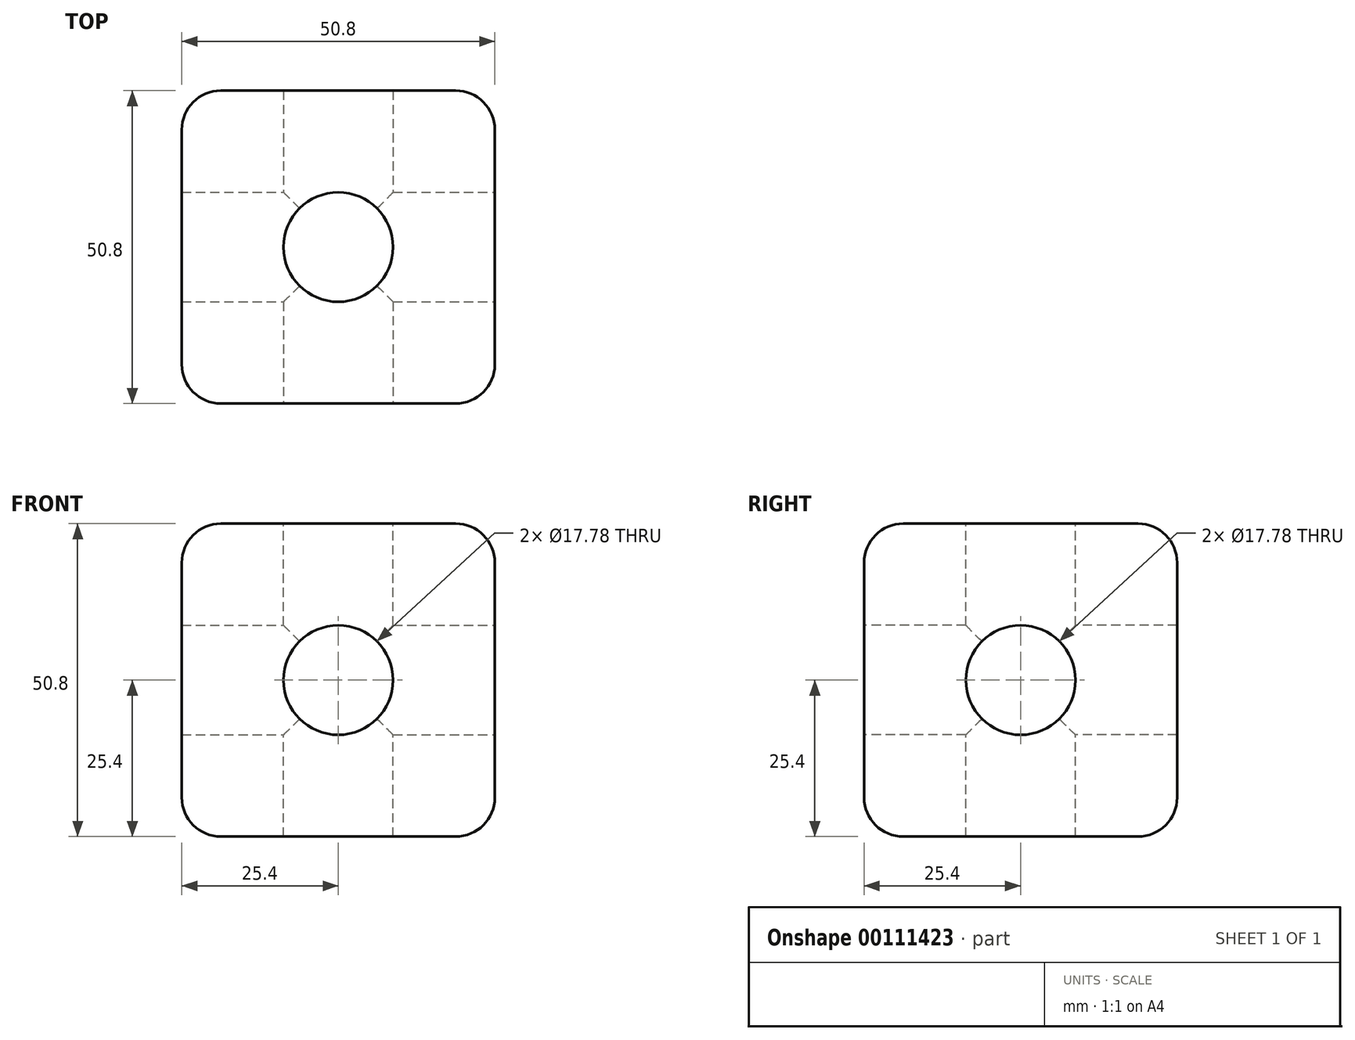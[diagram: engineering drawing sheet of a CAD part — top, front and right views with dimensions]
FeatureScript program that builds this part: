
annotation { "Feature Type Name" : "Feature", "Feature Type Description" : "" }
export const myFeature = defineFeature(function(context is Context, id is Id, definition is map)
    precondition{}
    {
        {
            var Q0;
            Q0=qCreatedBy(makeId("Front.planeOp"),FACE);
            var sketch = newSketch(context, id + "F0", { "sketchPlane" : qUnion([Q0])});
            skLineSegment(sketch, "E0.bottom", {"start": v(-25.4, 25.4) * mm, "end": v(25.4, 25.4) * mm});
            skLineSegment(sketch, "E0.top", {"start": v(-25.4, -25.4) * mm, "end": v(25.4, -25.4) * mm});
            skLineSegment(sketch, "E0.left", {"start": v(-25.4, 25.4) * mm, "end": v(-25.4, -25.4) * mm});
            skLineSegment(sketch, "E0.right", {"start": v(25.4, 25.4) * mm, "end": v(25.4, -25.4) * mm});
            skPoint(sketch, "E0.middle", {"position": v(0, 0) * mm});
            skSolve(sketch);
        }
        {
            var Q0;
            Q0=makeQuery(id+"F0.imprint","IMPRINT",FACE,{"disambiguationData":[TD([[makeQuery(id+"F0.imprint","IMPRINT",EDGE,{"derivedFrom":sQuery(id+"F0.wireOp",EDGE,"E0.bottom")}),-1.0]])]});
            extrude(context, id + "F1", {"entities" : qUnion([Q0]), "endBound" : BoundingType.SYMMETRIC, "depth" : 50.8 * mm});
        }
        {
            var Q0;
            Q0=makeQuery(id+"F1.opExtrude","CAP_EDGE",EDGE,{"disambiguationData":[OSD([sQuery(id+"F0.wireOp",EDGE,"E0.bottom")])],"isStart":false});
            var Q1;
            Q1=makeQuery(id+"F1.opExtrude","SWEPT_EDGE",EDGE,{"disambiguationData":[OSD([sQuery(id+"F0.wireOp",EDGE,"E0.bottom"),sQuery(id+"F0.wireOp",EDGE,"E0.right")])]});
            var Q2;
            Q2=makeQuery(id+"F1.opExtrude","SWEPT_EDGE",EDGE,{"disambiguationData":[OSD([sQuery(id+"F0.wireOp",EDGE,"E0.top"),sQuery(id+"F0.wireOp",EDGE,"E0.right")])]});
            var Q3;
            Q3=makeQuery(id+"F1.opExtrude","CAP_EDGE",EDGE,{"disambiguationData":[OSD([sQuery(id+"F0.wireOp",EDGE,"E0.top")])],"isStart":false});
            var Q4;
            Q4=makeQuery(id+"F1.opExtrude","CAP_EDGE",EDGE,{"disambiguationData":[OSD([sQuery(id+"F0.wireOp",EDGE,"E0.right")])],"isStart":false});
            var Q5;
            Q5=makeQuery(id+"F1.opExtrude","CAP_EDGE",EDGE,{"disambiguationData":[OSD([sQuery(id+"F0.wireOp",EDGE,"E0.bottom")])],"isStart":true});
            var Q6;
            Q6=makeQuery(id+"F1.opExtrude","SWEPT_FACE",FACE,{"disambiguationData":[OSD([sQuery(id+"F0.wireOp",EDGE,"E0.bottom")])]});
            var Q7;
            Q7=makeQuery(id+"F1.opExtrude","CAP_EDGE",EDGE,{"disambiguationData":[OSD([sQuery(id+"F0.wireOp",EDGE,"E0.right")])],"isStart":true});
            var Q8;
            Q8=makeQuery(id+"F1.opExtrude","CAP_EDGE",EDGE,{"disambiguationData":[OSD([sQuery(id+"F0.wireOp",EDGE,"E0.left")])],"isStart":false});
            var Q9;
            Q9=makeQuery(id+"F1.opExtrude","SWEPT_EDGE",EDGE,{"disambiguationData":[OSD([sQuery(id+"F0.wireOp",EDGE,"E0.top"),sQuery(id+"F0.wireOp",EDGE,"E0.left")])]});
            var Q10;
            Q10=makeQuery(id+"F1.opExtrude","CAP_EDGE",EDGE,{"disambiguationData":[OSD([sQuery(id+"F0.wireOp",EDGE,"E0.left")])],"isStart":true});
            var Q11;
            Q11=makeQuery(id+"F1.opExtrude","SWEPT_FACE",FACE,{"disambiguationData":[OSD([sQuery(id+"F0.wireOp",EDGE,"E0.top")])]});
            fillet(context, id + "F2", {"entities" : qUnion([Q0, Q1, Q2, Q3, Q4, Q5, Q6, Q7, Q8, Q9, Q10, Q11]), "radius" : 6.35 * mm, "tangentPropagation" : true, "allowEdgeOverflow" : false});
        }
        {
            var Q0;
            Q0=makeQuery(id+"F1.opExtrude","SWEPT_FACE",FACE,{"disambiguationData":[OSD([sQuery(id+"F0.wireOp",EDGE,"E0.bottom")])]});
            var sketch = newSketch(context, id + "F3", { "sketchPlane" : qUnion([Q0])});
            skCircle(sketch, "E1", {"center": v(0, 0) * mm, "radius": 8.89 * mm});
            skSolve(sketch);
        }
        {
            var Q0;
            Q0=makeQuery(id+"F3.imprint","IMPRINT",FACE,{"disambiguationData":[TD([[makeQuery(id+"F3.imprint","IMPRINT",EDGE,{"derivedFrom":sQuery(id+"F3.wireOp",EDGE,"E1")}),1.0]])]});
            var Q1;
            Q1=makeQuery(id+"F1.opExtrude","SWEPT_FACE",FACE,{"disambiguationData":[OSD([sQuery(id+"F0.wireOp",EDGE,"E0.top")])]});
            extrude(context, id + "F4", {"entities" : qUnion([Q0]), "operationType" : NewBodyOperationType.REMOVE, "endBound" : BoundingType.UP_TO_SURFACE, "oppositeDirection" : true, "endBoundEntityFace" : qUnion([Q1]), "depth" : 25.4 * mm});
        }
        {
            var Q0;
            Q0=makeQuery(id+"F1.opExtrude","CAP_FACE",FACE,{"disambiguationData":[OSD([sQuery(id+"F0.wireOp",EDGE,"E0.bottom"),sQuery(id+"F0.wireOp",EDGE,"E0.top"),sQuery(id+"F0.wireOp",EDGE,"E0.left"),sQuery(id+"F0.wireOp",EDGE,"E0.right")])],"isStart":false});
            var sketch = newSketch(context, id + "F5", { "sketchPlane" : qUnion([Q0])});
            skCircle(sketch, "E2", {"center": v(0, 0) * mm, "radius": 8.9 * mm});
            skSolve(sketch);
        }
        {
            var Q0;
            Q0=makeQuery(id+"F5.imprint","IMPRINT",FACE,{"disambiguationData":[TD([[makeQuery(id+"F5.imprint","IMPRINT",EDGE,{"derivedFrom":sQuery(id+"F5.wireOp",EDGE,"E2")}),1.0]])]});
            var Q1;
            Q1=makeQuery(id+"F1.opExtrude","CAP_FACE",FACE,{"disambiguationData":[OSD([sQuery(id+"F0.wireOp",EDGE,"E0.bottom"),sQuery(id+"F0.wireOp",EDGE,"E0.top"),sQuery(id+"F0.wireOp",EDGE,"E0.left"),sQuery(id+"F0.wireOp",EDGE,"E0.right")])],"isStart":true});
            extrude(context, id + "F6", {"entities" : qUnion([Q0]), "operationType" : NewBodyOperationType.REMOVE, "endBound" : BoundingType.UP_TO_SURFACE, "oppositeDirection" : true, "endBoundEntityFace" : qUnion([Q1]), "depth" : 25.4 * mm});
        }
        {
            var Q0;
            Q0=makeQuery(id+"F1.opExtrude","SWEPT_FACE",FACE,{"disambiguationData":[OSD([sQuery(id+"F0.wireOp",EDGE,"E0.right")])]});
            var sketch = newSketch(context, id + "F7", { "sketchPlane" : qUnion([Q0])});
            skCircle(sketch, "E3", {"center": v(0, 0) * mm, "radius": 8.9 * mm});
            skSolve(sketch);
        }
        {
            var Q0;
            Q0=makeQuery(id+"F7.imprint","IMPRINT",FACE,{"disambiguationData":[TD([[makeQuery(id+"F7.imprint","IMPRINT",EDGE,{"derivedFrom":sQuery(id+"F7.wireOp",EDGE,"E3")}),1.0]])]});
            var Q1;
            Q1=makeQuery(id+"F1.opExtrude","SWEPT_FACE",FACE,{"disambiguationData":[OSD([sQuery(id+"F0.wireOp",EDGE,"E0.left")])]});
            extrude(context, id + "F8", {"entities" : qUnion([Q0]), "operationType" : NewBodyOperationType.REMOVE, "endBound" : BoundingType.UP_TO_SURFACE, "oppositeDirection" : true, "endBoundEntityFace" : qUnion([Q1]), "depth" : 25.4 * mm});
        }
    });
